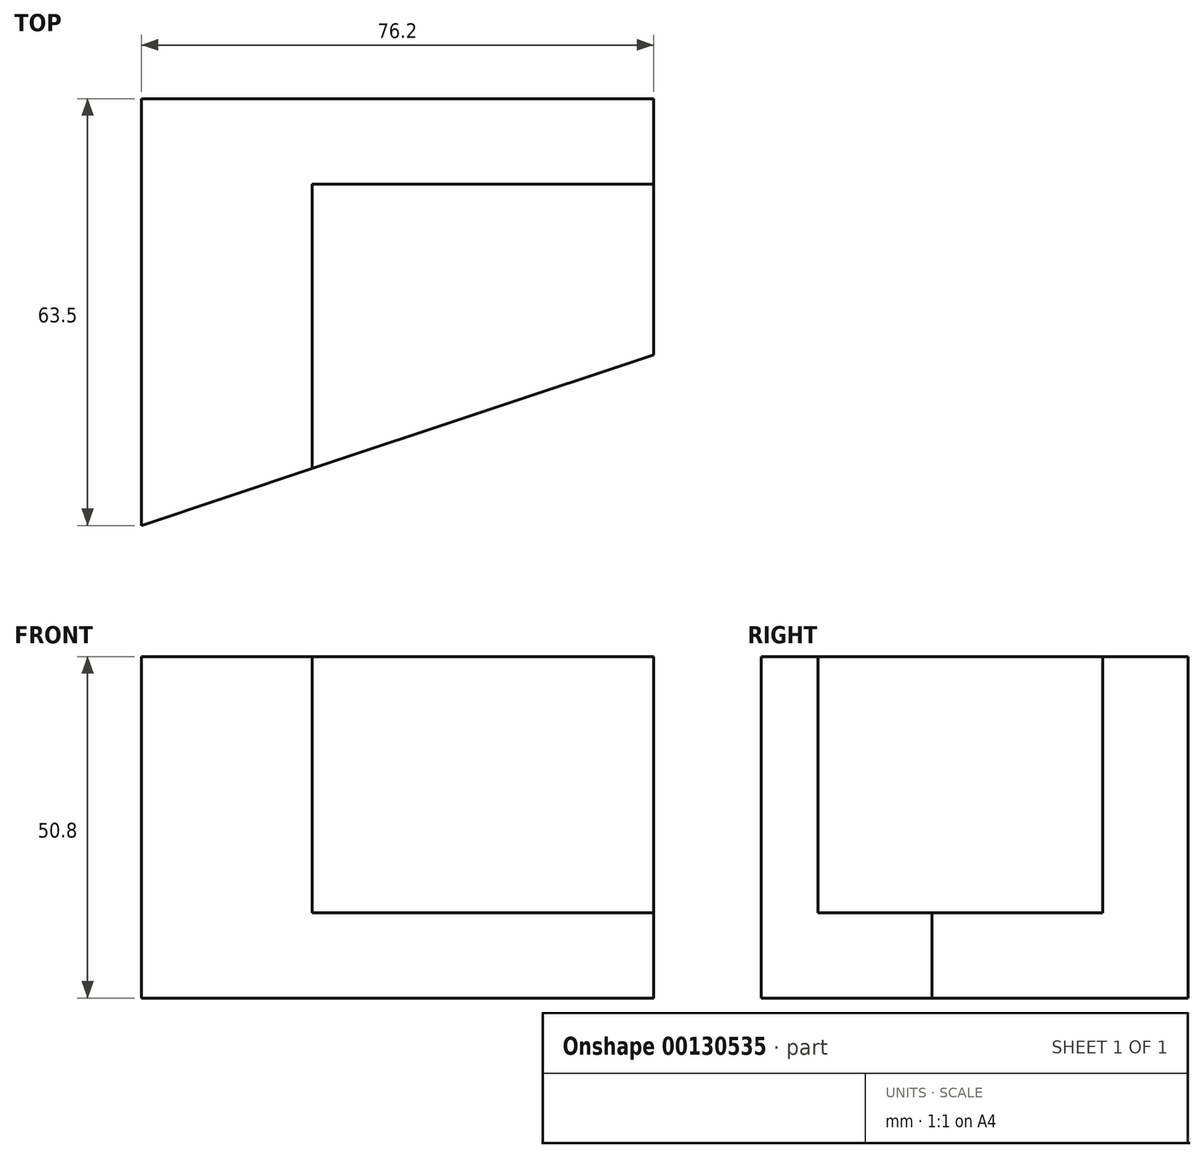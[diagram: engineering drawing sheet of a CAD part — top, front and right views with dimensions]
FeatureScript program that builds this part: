
annotation { "Feature Type Name" : "Feature", "Feature Type Description" : "" }
export const myFeature = defineFeature(function(context is Context, id is Id, definition is map)
    precondition{}
    {
        {
            var Q0;
            Q0=qCreatedBy(makeId("Front.planeOp"),FACE);
            var sketch = newSketch(context, id + "F0", { "sketchPlane" : qUnion([Q0])});
            skLineSegment(sketch, "E0.bottom", {"start": v(0, 0) * mm, "end": v(-76.2, 0) * mm});
            skLineSegment(sketch, "E0.top", {"start": v(0, 50.8) * mm, "end": v(-76.2, 50.8) * mm});
            skLineSegment(sketch, "E0.left", {"start": v(0, 0) * mm, "end": v(0, 50.8) * mm});
            skLineSegment(sketch, "E0.right", {"start": v(-76.2, 0) * mm, "end": v(-76.2, 50.8) * mm});
            skSolve(sketch);
        }
        {
            var Q0;
            Q0 = qSketchRegion(id + "F0", true);
            extrude(context, id + "F1", {"entities" : qUnion([Q0]), "oppositeDirection" : true, "depth" : 63.5 * mm});
        }
        {
            var Q0;
            Q0=makeQuery(id+"F1.opExtrude","CAP_FACE",FACE,{"disambiguationData":[OSD([sQuery(id+"F0.wireOp",EDGE,"E0.bottom"),sQuery(id+"F0.wireOp",EDGE,"E0.top"),sQuery(id+"F0.wireOp",EDGE,"E0.left"),sQuery(id+"F0.wireOp",EDGE,"E0.right")])],"isStart":true});
            var sketch = newSketch(context, id + "F2", { "sketchPlane" : qUnion([Q0])});
            skLineSegment(sketch, "E1.bottom", {"start": v(0, 50.8) * mm, "end": v(-50.8, 50.8) * mm});
            skLineSegment(sketch, "E1.top", {"start": v(0, 12.7) * mm, "end": v(-50.8, 12.7) * mm});
            skLineSegment(sketch, "E1.left", {"start": v(0, 50.8) * mm, "end": v(0, 12.7) * mm});
            skLineSegment(sketch, "E1.right", {"start": v(-50.8, 50.8) * mm, "end": v(-50.8, 12.7) * mm});
            skSolve(sketch);
        }
        {
            var Q0;
            Q0 = qSketchRegion(id + "F2", true);
            extrude(context, id + "F3", {"entities" : qUnion([Q0]), "operationType" : NewBodyOperationType.REMOVE, "oppositeDirection" : true, "depth" : 50.8 * mm});
        }
        {
            var Q0;
            Q0=makeQuery(id+"F1.opExtrude","SWEPT_FACE",FACE,{"disambiguationData":[OSD([sQuery(id+"F0.wireOp",EDGE,"E0.top")])]});
            var sketch = newSketch(context, id + "F4", { "sketchPlane" : qUnion([Q0])});
            skLineSegment(sketch, "E2", {"start": v(-76.2, 0) * mm, "end": v(0, 25.4) * mm});
            skLineSegment(sketch, "E3", {"start": v(0, 25.4) * mm, "end": v(0, 0) * mm});
            skLineSegment(sketch, "E4", {"start": v(0, 0) * mm, "end": v(-76.2, 0) * mm});
            skSolve(sketch);
        }
        {
            var Q0;
            Q0 = qSketchRegion(id + "F4", true);
            extrude(context, id + "F5", {"entities" : qUnion([Q0]), "operationType" : NewBodyOperationType.REMOVE, "endBound" : BoundingType.THROUGH_ALL, "oppositeDirection" : true, "depth" : 25.4 * mm});
        }
    });
